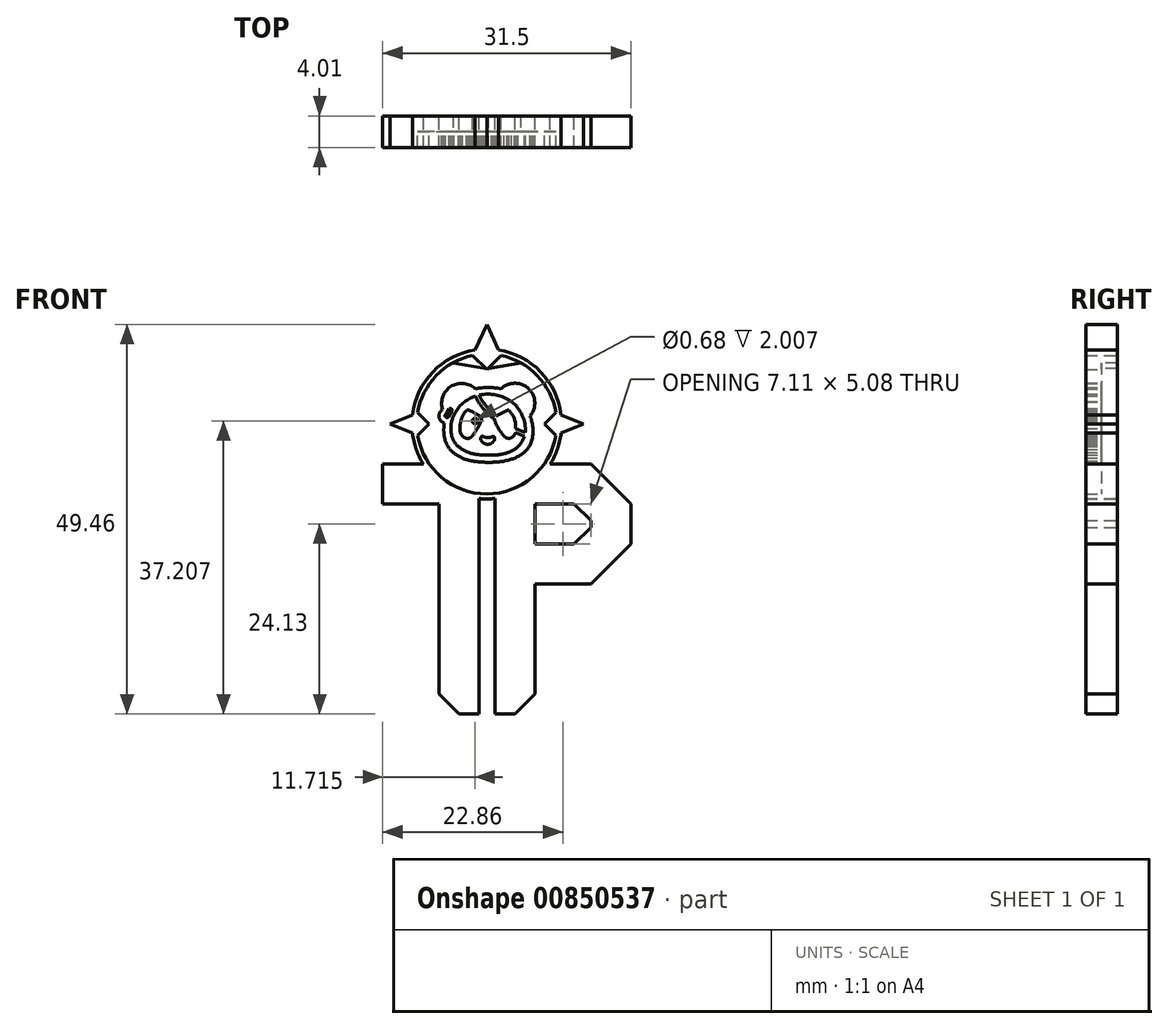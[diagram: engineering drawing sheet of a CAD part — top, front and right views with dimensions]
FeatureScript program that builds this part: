
annotation { "Feature Type Name" : "Feature", "Feature Type Description" : "" }
export const myFeature = defineFeature(function(context is Context, id is Id, definition is map)
    precondition{}
    {
        {
            var Q0;
            Q0=qCreatedBy(makeId("Front.planeOp"),FACE);
            var sketch = newSketch(context, id + "F0", { "sketchPlane" : qUnion([Q0])});
            skLineSegment(sketch, "E0.bottom", {"start": v(0, 0) * mm, "end": v(26.42, 0) * mm});
            skLineSegment(sketch, "E0.top", {"start": v(0, 31.75) * mm, "end": v(26.42, 31.75) * mm});
            skLineSegment(sketch, "E0.left", {"start": v(0, 0) * mm, "end": v(0, 31.75) * mm});
            skLineSegment(sketch, "E0.right", {"start": v(26.42, 0) * mm, "end": v(26.42, 16.5) * mm});
            skLineSegment(sketch, "E1", {"start": v(13.2, 31.75) * mm, "end": v(13.2, 0) * mm});
            skLineSegment(sketch, "E2", {"start": v(0, 26.67) * mm, "end": v(7.11, 26.67) * mm});
            skLineSegment(sketch, "E3", {"start": v(7.11, 26.67) * mm, "end": v(7.11, 0) * mm});
            skLineSegment(sketch, "E4", {"start": v(12.2, 31.75) * mm, "end": v(12.2, 0) * mm});
            skLineSegment(sketch, "E5", {"start": v(14.22, 31.75) * mm, "end": v(14.22, 0) * mm});
            skLineSegment(sketch, "E6", {"start": v(19.3, 31.75) * mm, "end": v(19.3, 0) * mm});
            skLineSegment(sketch, "E7", {"start": v(26.42, 31.75) * mm, "end": v(31.5, 26.67) * mm});
            skLineSegment(sketch, "E8", {"start": v(31.5, 26.67) * mm, "end": v(31.5, 21.59) * mm});
            skLineSegment(sketch, "E9", {"start": v(31.5, 21.59) * mm, "end": v(26.42, 16.5) * mm});
            skLineSegment(sketch, "E10", {"start": v(26.42, 16.5) * mm, "end": v(19.3, 16.5) * mm});
            skLineSegment(sketch, "E11", {"start": v(24.31, 26.67) * mm, "end": v(19.3, 26.67) * mm});
            skLineSegment(sketch, "E12", {"start": v(24.31, 21.59) * mm, "end": v(19.3, 21.59) * mm});
            skLineSegment(sketch, "E13.trimOffspring", {"start": v(26.42, 23.7) * mm, "end": v(26.42, 24.57) * mm});
            skLineSegment(sketch, "E14", {"start": v(24.31, 26.67) * mm, "end": v(26.42, 24.57) * mm});
            skLineSegment(sketch, "E15", {"start": v(24.31, 21.59) * mm, "end": v(26.42, 23.7) * mm});
            skPoint(sketch, "E16.orphan", {"position": v(26.42, 26.67) * mm});
            skPoint(sketch, "E17.orphan", {"position": v(26.42, 21.59) * mm});
            skLineSegment(sketch, "E18", {"start": v(0, 26.67) * mm, "end": v(0, 31.75) * mm});
            skLineSegment(sketch, "E19", {"start": v(0, 29.2) * mm, "end": v(2.54, 26.67) * mm});
            skLineSegment(sketch, "E20", {"start": v(7.11, 0) * mm, "end": v(12.2, 0) * mm});
            skLineSegment(sketch, "E21", {"start": v(14.22, 0) * mm, "end": v(19.3, 0) * mm});
            skLineSegment(sketch, "E22", {"start": v(9.65, 0) * mm, "end": v(7.11, 2.54) * mm});
            skLineSegment(sketch, "E23", {"start": v(16.76, 0) * mm, "end": v(19.3, 2.54) * mm});
            skCircle(sketch, "E24", {"center": v(13.2, 36.83) * mm, "radius": 9.53 * mm});
            skSolve(sketch);
        }
        {
            var Q0;
            {var subQ0=sQuery(id+"F0.wireOp",EDGE,"E24");var subQ1=sQuery(id+"F0.wireOp",EDGE,"E0.top");var subQ7=makeQuery(id+"F0.imprint","INTERSECT",VERTEX,{"disambiguationData":[OD(0.0)],"derivedFrom":[subQ1,subQ0]});Q0=makeQuery(id+"F0.imprint","IMPRINT",FACE,{"disambiguationData":[TD([[makeQuery(id+"F0.imprint","IMPRINT",EDGE,{"disambiguationData":[TD([[subQ7,-1.0]])],"derivedFrom":subQ1}),1.0]])]});}
            var Q1;
            {var subQ0=sQuery(id+"F0.wireOp",EDGE,"E24");var subQ1=sQuery(id+"F0.wireOp",EDGE,"E0.top");var subQ2=makeQuery(id+"F0.imprint","INTERSECT",VERTEX,{"disambiguationData":[OD(0.0)],"derivedFrom":[subQ1,subQ0]});Q1=makeQuery(id+"F0.imprint","IMPRINT",FACE,{"disambiguationData":[TD([[makeQuery(id+"F0.imprint","IMPRINT",EDGE,{"disambiguationData":[TD([[subQ2,-1.0]])],"derivedFrom":subQ1}),-1.0]])]});}
            var Q2;
            {var subQ0=sQuery(id+"F0.wireOp",EDGE,"E5");var subQ1=sQuery(id+"F0.wireOp",EDGE,"E0.top");var subQ2=makeQuery(id+"F0.imprint","INTERSECT",VERTEX,{"derivedFrom":[subQ1,subQ0]});Q2=makeQuery(id+"F0.imprint","IMPRINT",FACE,{"disambiguationData":[TD([[makeQuery(id+"F0.imprint","IMPRINT",EDGE,{"disambiguationData":[TD([[subQ2,-1.0]])],"derivedFrom":subQ1}),-1.0]])]});}
            var Q3;
            {var subQ0=sQuery(id+"F0.wireOp",EDGE,"E4");var subQ1=sQuery(id+"F0.wireOp",EDGE,"E0.top");var subQ2=makeQuery(id+"F0.imprint","INTERSECT",VERTEX,{"derivedFrom":[subQ1,subQ0]});Q3=makeQuery(id+"F0.imprint","IMPRINT",FACE,{"disambiguationData":[TD([[makeQuery(id+"F0.imprint","IMPRINT",EDGE,{"disambiguationData":[TD([[subQ2,-1.0]])],"derivedFrom":subQ1}),-1.0]])]});}
            var Q4;
            {var subQ0=sQuery(id+"F0.wireOp",EDGE,"E5");var subQ1=sQuery(id+"F0.wireOp",EDGE,"E0.top");var subQ2=makeQuery(id+"F0.imprint","INTERSECT",VERTEX,{"derivedFrom":[subQ1,subQ0]});Q4=makeQuery(id+"F0.imprint","IMPRINT",FACE,{"disambiguationData":[TD([[makeQuery(id+"F0.imprint","IMPRINT",EDGE,{"disambiguationData":[TD([[subQ2,1.0]])],"derivedFrom":subQ1}),-1.0]])]});}
            var Q5;
            {var subQ0=sQuery(id+"F0.wireOp",EDGE,"E19");Q5=makeQuery(id+"F0.imprint","IMPRINT",FACE,{"disambiguationData":[TD([[makeQuery(id+"F0.imprint","IMPRINT",EDGE,{"derivedFrom":subQ0}),1.0]])]});}
            var Q6;
            {var subQ8=sQuery(id+"F0.wireOp",EDGE,"E23");Q6=makeQuery(id+"F0.imprint","IMPRINT",FACE,{"disambiguationData":[TD([[makeQuery(id+"F0.imprint","IMPRINT",EDGE,{"derivedFrom":subQ8}),1.0]])]});}
            var Q7;
            {var subQ3=sQuery(id+"F0.wireOp",EDGE,"E7");Q7=makeQuery(id+"F0.imprint","IMPRINT",FACE,{"disambiguationData":[TD([[makeQuery(id+"F0.imprint","IMPRINT",EDGE,{"derivedFrom":subQ3}),-1.0]])]});}
            var Q8;
            {var subQ0=sQuery(id+"F0.wireOp",EDGE,"E24");var subQ1=sQuery(id+"F0.wireOp",EDGE,"E0.top");var subQ2=makeQuery(id+"F0.imprint","INTERSECT",VERTEX,{"disambiguationData":[OD(1.0)],"derivedFrom":[subQ1,subQ0]});Q8=makeQuery(id+"F0.imprint","IMPRINT",FACE,{"disambiguationData":[TD([[makeQuery(id+"F0.imprint","IMPRINT",EDGE,{"disambiguationData":[TD([[subQ2,1.0]])],"derivedFrom":subQ1}),-1.0]])]});}
            var Q9;
            {var subQ0=sQuery(id+"F0.wireOp",EDGE,"E19");Q9=makeQuery(id+"F0.imprint","IMPRINT",FACE,{"disambiguationData":[TD([[makeQuery(id+"F0.imprint","IMPRINT",EDGE,{"derivedFrom":subQ0}),-1.0]])]});}
            extrude(context, id + "F1", {"entities" : qUnion([Q0, Q1, Q2, Q3, Q4, Q5, Q6, Q7, Q8, Q9]), "depth" : 2 * mm, "offsetDistance" : 25.4 * mm});
        }
        {
            var Q0;
            Q0=makeQuery(id+"F1.opExtrude","CAP_FACE",FACE,{"disambiguationData":[OSD([sQuery(id+"F0.wireOp",EDGE,"E0.bottom"),sQuery(id+"F0.wireOp",EDGE,"E0.top"),sQuery(id+"F0.wireOp",EDGE,"E0.left"),sQuery(id+"F0.wireOp",EDGE,"E2"),sQuery(id+"F0.wireOp",EDGE,"E3"),sQuery(id+"F0.wireOp",EDGE,"E4"),sQuery(id+"F0.wireOp",EDGE,"E5"),sQuery(id+"F0.wireOp",EDGE,"E6"),sQuery(id+"F0.wireOp",EDGE,"E7"),sQuery(id+"F0.wireOp",EDGE,"E8"),sQuery(id+"F0.wireOp",EDGE,"E9"),sQuery(id+"F0.wireOp",EDGE,"E10"),sQuery(id+"F0.wireOp",EDGE,"E11"),sQuery(id+"F0.wireOp",EDGE,"E12"),sQuery(id+"F0.wireOp",EDGE,"E13.trimOffspring"),sQuery(id+"F0.wireOp",EDGE,"E14"),sQuery(id+"F0.wireOp",EDGE,"E15"),sQuery(id+"F0.wireOp",EDGE,"E22"),sQuery(id+"F0.wireOp",EDGE,"E23"),sQuery(id+"F0.wireOp",EDGE,"E24")])],"isStart":false});
            var sketch = newSketch(context, id + "F2", { "sketchPlane" : qUnion([Q0])});
            skLineSegment(sketch, "E25.bottom", {"start": v(0, 0) * mm, "end": v(26.42, 0) * mm});
            skLineSegment(sketch, "E25.top", {"start": v(0, 31.75) * mm, "end": v(26.42, 31.75) * mm});
            skLineSegment(sketch, "E25.left", {"start": v(0, 0) * mm, "end": v(0, 31.75) * mm});
            skLineSegment(sketch, "E25.right", {"start": v(26.42, 0) * mm, "end": v(26.42, 16.5) * mm});
            skLineSegment(sketch, "E26", {"start": v(13.2, 31.75) * mm, "end": v(13.2, 0) * mm});
            skLineSegment(sketch, "E27", {"start": v(0, 26.67) * mm, "end": v(7.11, 26.67) * mm});
            skLineSegment(sketch, "E28", {"start": v(7.11, 26.67) * mm, "end": v(7.11, 0) * mm});
            skLineSegment(sketch, "E29", {"start": v(12.2, 31.75) * mm, "end": v(12.2, 0) * mm});
            skLineSegment(sketch, "E30", {"start": v(14.22, 31.75) * mm, "end": v(14.22, 0) * mm});
            skLineSegment(sketch, "E31", {"start": v(19.3, 31.75) * mm, "end": v(19.3, 0) * mm});
            skLineSegment(sketch, "E32", {"start": v(26.42, 31.75) * mm, "end": v(31.5, 26.67) * mm});
            skLineSegment(sketch, "E33", {"start": v(31.5, 26.67) * mm, "end": v(31.5, 21.59) * mm});
            skLineSegment(sketch, "E34", {"start": v(31.5, 21.59) * mm, "end": v(26.42, 16.5) * mm});
            skLineSegment(sketch, "E35", {"start": v(26.42, 16.5) * mm, "end": v(19.3, 16.5) * mm});
            skLineSegment(sketch, "E36", {"start": v(24.31, 26.67) * mm, "end": v(19.3, 26.67) * mm});
            skLineSegment(sketch, "E37", {"start": v(24.31, 21.59) * mm, "end": v(19.3, 21.59) * mm});
            skLineSegment(sketch, "E38.trimOffspring", {"start": v(26.42, 23.7) * mm, "end": v(26.42, 24.57) * mm});
            skLineSegment(sketch, "E39", {"start": v(24.31, 26.67) * mm, "end": v(26.42, 24.57) * mm});
            skLineSegment(sketch, "E40", {"start": v(24.31, 21.59) * mm, "end": v(26.42, 23.7) * mm});
            skPoint(sketch, "E41.orphan", {"position": v(26.42, 26.67) * mm});
            skPoint(sketch, "E42.orphan", {"position": v(26.42, 21.59) * mm});
            skLineSegment(sketch, "E43", {"start": v(0, 26.67) * mm, "end": v(0, 31.75) * mm});
            skLineSegment(sketch, "E44", {"start": v(0, 29.2) * mm, "end": v(2.54, 26.67) * mm});
            skLineSegment(sketch, "E45", {"start": v(7.11, 0) * mm, "end": v(12.2, 0) * mm});
            skLineSegment(sketch, "E46", {"start": v(14.22, 0) * mm, "end": v(19.3, 0) * mm});
            skLineSegment(sketch, "E47", {"start": v(9.65, 0) * mm, "end": v(7.11, 2.54) * mm});
            skLineSegment(sketch, "E48", {"start": v(16.76, 0) * mm, "end": v(19.3, 2.54) * mm});
            skCircle(sketch, "E49", {"center": v(13.2, 36.83) * mm, "radius": 9.53 * mm});
            skArc(sketch, "E50", {"start": v(6.4, 36) * mm, "mid": v(6.22, 35.67) * mm, "end": v(6.11, 35.3) * mm});
            skArc(sketch, "E51", {"start": v(6.11, 35.3) * mm, "mid": v(6.1, 35.08) * mm, "end": v(6.16, 34.85) * mm});
            skArc(sketch, "E52", {"start": v(6.16, 34.85) * mm, "mid": v(6.22, 34.79) * mm, "end": v(6.3, 34.77) * mm});
            skArc(sketch, "E53", {"start": v(6.3, 34.77) * mm, "mid": v(6.4, 34.81) * mm, "end": v(6.47, 34.9) * mm});
            skArc(sketch, "E54", {"start": v(6.88, 35.33) * mm, "mid": v(6.66, 35.14) * mm, "end": v(6.47, 34.9) * mm});
            skArc(sketch, "E55", {"start": v(7.24, 35.54) * mm, "mid": v(7.06, 35.45) * mm, "end": v(6.88, 35.33) * mm});
            skArc(sketch, "E56", {"start": v(7.7, 35.67) * mm, "mid": v(7.47, 35.61) * mm, "end": v(7.24, 35.54) * mm});
            skArc(sketch, "E57", {"start": v(9.2, 36.34) * mm, "mid": v(8.98, 36.2) * mm, "end": v(8.78, 36.05) * mm});
            skArc(sketch, "E58", {"start": v(9.2, 36.34) * mm, "mid": v(9.36, 36.41) * mm, "end": v(9.52, 36.5) * mm});
            skArc(sketch, "E59", {"start": v(9.52, 36.5) * mm, "mid": v(10.37, 36.37) * mm, "end": v(11.23, 36.4) * mm});
            skArc(sketch, "E60", {"start": v(11.23, 36.4) * mm, "mid": v(11.72, 36.48) * mm, "end": v(12.19, 36.65) * mm});
            skArc(sketch, "E61", {"start": v(12.19, 36.65) * mm, "mid": v(12.45, 36.8) * mm, "end": v(12.66, 37.03) * mm});
            skArc(sketch, "E62", {"start": v(11.55, 37.03) * mm, "mid": v(12.1, 37.01) * mm, "end": v(12.66, 37.03) * mm});
            skArc(sketch, "E63", {"start": v(11.07, 37.17) * mm, "mid": v(11.3, 37.08) * mm, "end": v(11.55, 37.03) * mm});
            skArc(sketch, "E64", {"start": v(10.85, 37.36) * mm, "mid": v(10.95, 37.25) * mm, "end": v(11.07, 37.17) * mm});
            skArc(sketch, "E65", {"start": v(12.47, 37.67) * mm, "mid": v(11.65, 37.56) * mm, "end": v(10.85, 37.36) * mm});
            skArc(sketch, "E66", {"start": v(14.27, 37.6) * mm, "mid": v(13.38, 37.7) * mm, "end": v(12.47, 37.67) * mm});
            skArc(sketch, "E67", {"start": v(16.2, 36.98) * mm, "mid": v(15.26, 37.36) * mm, "end": v(14.27, 37.6) * mm});
            skArc(sketch, "E68", {"start": v(17.82, 36) * mm, "mid": v(17.02, 36.51) * mm, "end": v(16.2, 36.98) * mm});
            skArc(sketch, "E69", {"start": v(18.3, 35.54) * mm, "mid": v(18.08, 35.79) * mm, "end": v(17.82, 36) * mm});
            skArc(sketch, "E70", {"start": v(18.3, 35.54) * mm, "mid": v(18.28, 35.11) * mm, "end": v(18.33, 34.7) * mm});
            skArc(sketch, "E71", {"start": v(18.33, 34.7) * mm, "mid": v(18.49, 34.23) * mm, "end": v(18.74, 33.8) * mm});
            skArc(sketch, "E72", {"start": v(18.74, 33.8) * mm, "mid": v(18.9, 33.62) * mm, "end": v(19.08, 33.46) * mm});
            skArc(sketch, "E73", {"start": v(19.08, 33.46) * mm, "mid": v(19.2, 33.62) * mm, "end": v(19.3, 33.8) * mm});
            skArc(sketch, "E74", {"start": v(19.3, 33.8) * mm, "mid": v(19.42, 34.13) * mm, "end": v(19.47, 34.48) * mm});
            skArc(sketch, "E75", {"start": v(19.47, 34.48) * mm, "mid": v(19.48, 34.72) * mm, "end": v(19.47, 34.95) * mm});
            skArc(sketch, "E76", {"start": v(19.47, 34.95) * mm, "mid": v(19.88, 34.96) * mm, "end": v(20.3, 35) * mm});
            skArc(sketch, "E77", {"start": v(20.3, 35) * mm, "mid": v(20.67, 35.07) * mm, "end": v(21.02, 35.2) * mm});
            skArc(sketch, "E78", {"start": v(21.02, 35.2) * mm, "mid": v(21.2, 35.32) * mm, "end": v(21.35, 35.48) * mm});
            skArc(sketch, "E79", {"start": v(21.35, 35.48) * mm, "mid": v(20.95, 35.65) * mm, "end": v(20.53, 35.79) * mm});
            skArc(sketch, "E80", {"start": v(20.53, 35.79) * mm, "mid": v(20.12, 35.96) * mm, "end": v(19.7, 36.1) * mm});
            skArc(sketch, "E81", {"start": v(19.7, 36.1) * mm, "mid": v(19.33, 36.15) * mm, "end": v(18.97, 36.1) * mm});
            skArc(sketch, "E82", {"start": v(18.74, 36.12) * mm, "mid": v(18.85, 36.09) * mm, "end": v(18.97, 36.1) * mm});
            skArc(sketch, "E83", {"start": v(18.38, 36.54) * mm, "mid": v(18.54, 36.31) * mm, "end": v(18.74, 36.12) * mm});
            skArc(sketch, "E84", {"start": v(18.38, 36.54) * mm, "mid": v(17.88, 37.34) * mm, "end": v(17.35, 38.12) * mm});
            skArc(sketch, "E85", {"start": v(17.35, 38.12) * mm, "mid": v(16.5, 38.98) * mm, "end": v(15.51, 39.69) * mm});
            skArc(sketch, "E86", {"start": v(15.51, 39.69) * mm, "mid": v(14.75, 40.1) * mm, "end": v(13.95, 40.42) * mm});
            skArc(sketch, "E87", {"start": v(13.49, 40.82) * mm, "mid": v(13.7, 40.6) * mm, "end": v(13.95, 40.42) * mm});
            skArc(sketch, "E88", {"start": v(13.4, 41.11) * mm, "mid": v(13.42, 40.96) * mm, "end": v(13.49, 40.82) * mm});
            skArc(sketch, "E89", {"start": v(13.57, 41.38) * mm, "mid": v(13.45, 41.27) * mm, "end": v(13.4, 41.11) * mm});
            skArc(sketch, "E90", {"start": v(13.57, 41.38) * mm, "mid": v(13.77, 41.52) * mm, "end": v(13.95, 41.68) * mm});
            skArc(sketch, "E91", {"start": v(13.95, 41.68) * mm, "mid": v(14.07, 41.84) * mm, "end": v(14.14, 42.03) * mm});
            skArc(sketch, "E92", {"start": v(14.14, 42.03) * mm, "mid": v(13.9, 42.08) * mm, "end": v(13.64, 42.09) * mm});
            skArc(sketch, "E93", {"start": v(13.64, 42.09) * mm, "mid": v(13.3, 42.07) * mm, "end": v(12.97, 42) * mm});
            skArc(sketch, "E94", {"start": v(12.97, 42) * mm, "mid": v(12.34, 41.75) * mm, "end": v(11.78, 41.38) * mm});
            skArc(sketch, "E95", {"start": v(11.78, 41.38) * mm, "mid": v(11.32, 40.98) * mm, "end": v(10.92, 40.5) * mm});
            skArc(sketch, "E96", {"start": v(10.92, 40.5) * mm, "mid": v(9.67, 40.25) * mm, "end": v(8.5, 39.73) * mm});
            skArc(sketch, "E97", {"start": v(8.5, 39.73) * mm, "mid": v(7.74, 39.11) * mm, "end": v(7.14, 38.35) * mm});
            skArc(sketch, "E98", {"start": v(7.14, 38.35) * mm, "mid": v(6.66, 37.56) * mm, "end": v(6.37, 36.7) * mm});
            skArc(sketch, "E99", {"start": v(6.37, 36.7) * mm, "mid": v(6.34, 36.35) * mm, "end": v(6.4, 36) * mm});
            skArc(sketch, "E100", {"start": v(8.47, 38.82) * mm, "mid": v(7.96, 38.3) * mm, "end": v(7.62, 37.67) * mm});
            skArc(sketch, "E101", {"start": v(9.85, 39.52) * mm, "mid": v(9.13, 39.23) * mm, "end": v(8.47, 38.82) * mm});
            skArc(sketch, "E102", {"start": v(11.05, 39.73) * mm, "mid": v(10.44, 39.66) * mm, "end": v(9.85, 39.52) * mm});
            skArc(sketch, "E103", {"start": v(8.43, 38.6) * mm, "mid": v(8, 38.16) * mm, "end": v(7.62, 37.67) * mm});
            skArc(sketch, "E104", {"start": v(9.45, 39.2) * mm, "mid": v(8.92, 38.94) * mm, "end": v(8.43, 38.6) * mm});
            skArc(sketch, "E105", {"start": v(11.05, 39.73) * mm, "mid": v(10.24, 39.5) * mm, "end": v(9.45, 39.2) * mm});
            skArc(sketch, "E106", {"start": v(7.7, 35.67) * mm, "mid": v(8.27, 35.77) * mm, "end": v(8.78, 36.05) * mm});
            skSolve(sketch);
        }
        {
            var Q0;
            {var subQ12=sQuery(id+"F2.wireOp",EDGE,"E44");Q0=makeQuery(id+"F2.imprint","IMPRINT",FACE,{"disambiguationData":[TD([[makeQuery(id+"F2.imprint","IMPRINT",EDGE,{"derivedFrom":subQ12}),1.0]])]});}
            var Q1;
            {var subQ6=sQuery(id+"F2.wireOp",EDGE,"E48");Q1=makeQuery(id+"F2.imprint","IMPRINT",FACE,{"disambiguationData":[TD([[makeQuery(id+"F2.imprint","IMPRINT",EDGE,{"derivedFrom":subQ6}),1.0]])]});}
            var Q2;
            {var subQ2=sQuery(id+"F2.wireOp",EDGE,"E32");Q2=makeQuery(id+"F2.imprint","IMPRINT",FACE,{"disambiguationData":[TD([[makeQuery(id+"F2.imprint","IMPRINT",EDGE,{"derivedFrom":subQ2}),-1.0]])]});}
            var Q3;
            {var subQ3=sQuery(id+"F2.wireOp",EDGE,"E44");Q3=makeQuery(id+"F2.imprint","IMPRINT",FACE,{"disambiguationData":[TD([[makeQuery(id+"F2.imprint","IMPRINT",EDGE,{"derivedFrom":subQ3}),-1.0]])]});}
            extrude(context, id + "F3", {"entities" : qUnion([Q0, Q1, Q2, Q3]), "operationType" : NewBodyOperationType.ADD, "depth" : 2 * mm, "offsetDistance" : 25.4 * mm});
        }
        {
            var Q0;
            Q0=makeQuery(id+"F1.opExtrude","CAP_FACE",FACE,{"disambiguationData":[OSD([sQuery(id+"F0.wireOp",EDGE,"E0.bottom"),sQuery(id+"F0.wireOp",EDGE,"E0.top"),sQuery(id+"F0.wireOp",EDGE,"E0.left"),sQuery(id+"F0.wireOp",EDGE,"E2"),sQuery(id+"F0.wireOp",EDGE,"E3"),sQuery(id+"F0.wireOp",EDGE,"E4"),sQuery(id+"F0.wireOp",EDGE,"E5"),sQuery(id+"F0.wireOp",EDGE,"E6"),sQuery(id+"F0.wireOp",EDGE,"E7"),sQuery(id+"F0.wireOp",EDGE,"E8"),sQuery(id+"F0.wireOp",EDGE,"E9"),sQuery(id+"F0.wireOp",EDGE,"E10"),sQuery(id+"F0.wireOp",EDGE,"E11"),sQuery(id+"F0.wireOp",EDGE,"E12"),sQuery(id+"F0.wireOp",EDGE,"E13.trimOffspring"),sQuery(id+"F0.wireOp",EDGE,"E14"),sQuery(id+"F0.wireOp",EDGE,"E15"),sQuery(id+"F0.wireOp",EDGE,"E22"),sQuery(id+"F0.wireOp",EDGE,"E23"),sQuery(id+"F0.wireOp",EDGE,"E24")])],"isStart":false});
            var sketch = newSketch(context, id + "F4", { "sketchPlane" : qUnion([Q0])});
            skLineSegment(sketch, "E107.bottom", {"start": v(0, 0) * mm, "end": v(26.42, 0) * mm});
            skLineSegment(sketch, "E107.top", {"start": v(0, 31.75) * mm, "end": v(26.42, 31.75) * mm});
            skLineSegment(sketch, "E107.left", {"start": v(0, 0) * mm, "end": v(0, 31.75) * mm});
            skLineSegment(sketch, "E107.right", {"start": v(26.42, 0) * mm, "end": v(26.42, 16.5) * mm});
            skLineSegment(sketch, "E108", {"start": v(13.2, 31.75) * mm, "end": v(13.2, 0) * mm});
            skLineSegment(sketch, "E109", {"start": v(0, 26.67) * mm, "end": v(7.11, 26.67) * mm});
            skLineSegment(sketch, "E110", {"start": v(7.11, 26.67) * mm, "end": v(7.11, 0) * mm});
            skLineSegment(sketch, "E111", {"start": v(12.2, 31.75) * mm, "end": v(12.2, 0) * mm});
            skLineSegment(sketch, "E112", {"start": v(14.22, 31.75) * mm, "end": v(14.22, 0) * mm});
            skLineSegment(sketch, "E113", {"start": v(19.3, 31.75) * mm, "end": v(19.3, 0) * mm});
            skLineSegment(sketch, "E114", {"start": v(26.42, 31.75) * mm, "end": v(31.5, 26.67) * mm});
            skLineSegment(sketch, "E115", {"start": v(31.5, 26.67) * mm, "end": v(31.5, 21.59) * mm});
            skLineSegment(sketch, "E116", {"start": v(31.5, 21.59) * mm, "end": v(26.42, 16.5) * mm});
            skLineSegment(sketch, "E117", {"start": v(26.42, 16.5) * mm, "end": v(19.3, 16.5) * mm});
            skLineSegment(sketch, "E118", {"start": v(24.31, 26.67) * mm, "end": v(19.3, 26.67) * mm});
            skLineSegment(sketch, "E119", {"start": v(24.31, 21.59) * mm, "end": v(19.3, 21.59) * mm});
            skLineSegment(sketch, "E120.trimOffspring", {"start": v(26.42, 23.7) * mm, "end": v(26.42, 24.57) * mm});
            skLineSegment(sketch, "E121", {"start": v(24.31, 26.67) * mm, "end": v(26.42, 24.57) * mm});
            skLineSegment(sketch, "E122", {"start": v(24.31, 21.59) * mm, "end": v(26.42, 23.7) * mm});
            skPoint(sketch, "E123.orphan", {"position": v(26.42, 26.67) * mm});
            skPoint(sketch, "E124.orphan", {"position": v(26.42, 21.59) * mm});
            skLineSegment(sketch, "E125", {"start": v(0, 26.67) * mm, "end": v(0, 31.75) * mm});
            skLineSegment(sketch, "E126", {"start": v(0, 29.2) * mm, "end": v(2.54, 26.67) * mm});
            skLineSegment(sketch, "E127", {"start": v(7.11, 0) * mm, "end": v(12.2, 0) * mm});
            skLineSegment(sketch, "E128", {"start": v(14.22, 0) * mm, "end": v(19.3, 0) * mm});
            skLineSegment(sketch, "E129", {"start": v(9.65, 0) * mm, "end": v(7.11, 2.54) * mm});
            skLineSegment(sketch, "E130", {"start": v(16.76, 0) * mm, "end": v(19.3, 2.54) * mm});
            skCircle(sketch, "E131", {"center": v(13.2, 36.83) * mm, "radius": 9.53 * mm});
            skCircle(sketch, "E132", {"center": v(13.2, 36.83) * mm, "radius": 8.9 * mm});
            skLineSegment(sketch, "E133", {"start": v(13.2, 36.83) * mm, "end": v(22.73, 36.83) * mm});
            skLineSegment(sketch, "E134", {"start": v(13.2, 36.83) * mm, "end": v(13.2, 46.35) * mm});
            skLineSegment(sketch, "E135", {"start": v(13.2, 36.83) * mm, "end": v(3.68, 36.83) * mm});
            skLineSegment(sketch, "E136", {"start": v(13.2, 43.74) * mm, "end": v(11.41, 45.54) * mm});
            skLineSegment(sketch, "E137", {"start": v(13.2, 43.74) * mm, "end": v(15, 45.54) * mm});
            skLineSegment(sketch, "E138", {"start": v(11.41, 45.54) * mm, "end": v(13.2, 49.46) * mm});
            skLineSegment(sketch, "E139", {"start": v(13.2, 49.46) * mm, "end": v(15, 45.54) * mm});
            skLineSegment(sketch, "E140", {"start": v(13.2, 49.46) * mm, "end": v(13.2, 46.35) * mm});
            skLineSegment(sketch, "E141", {"start": v(20.54, 36.83) * mm, "end": v(21.98, 38.27) * mm});
            skLineSegment(sketch, "E142", {"start": v(20.54, 36.83) * mm, "end": v(21.98, 35.4) * mm});
            skLineSegment(sketch, "E143", {"start": v(21.98, 38.27) * mm, "end": v(25.5, 36.83) * mm});
            skLineSegment(sketch, "E144", {"start": v(21.98, 35.4) * mm, "end": v(25.5, 36.83) * mm});
            skLineSegment(sketch, "E145", {"start": v(22.73, 36.83) * mm, "end": v(25.5, 36.83) * mm});
            skLineSegment(sketch, "E146", {"start": v(5.87, 36.83) * mm, "end": v(4.43, 38.27) * mm});
            skLineSegment(sketch, "E147", {"start": v(5.87, 36.83) * mm, "end": v(4.43, 35.4) * mm});
            skLineSegment(sketch, "E148", {"start": v(4.43, 35.4) * mm, "end": v(0.9, 36.83) * mm});
            skLineSegment(sketch, "E149", {"start": v(0.9, 36.83) * mm, "end": v(4.43, 38.27) * mm});
            skLineSegment(sketch, "E150", {"start": v(3.68, 36.83) * mm, "end": v(0.9, 36.83) * mm});
            skSolve(sketch);
        }
        {
            var Q0;
            {var subQ0=sQuery(id+"F4.wireOp",EDGE,"E138");var subQ1=sQuery(id+"F4.wireOp",EDGE,"E131");var subQ2=makeQuery(id+"F4.imprint","INTERSECT",VERTEX,{"derivedFrom":[subQ1,subQ0]});Q0=makeQuery(id+"F4.imprint","IMPRINT",FACE,{"disambiguationData":[TD([[makeQuery(id+"F4.imprint","IMPRINT",EDGE,{"disambiguationData":[TD([[subQ2,-1.0]])],"derivedFrom":subQ1}),1.0]])]});}
            var Q1;
            {var subQ0=sQuery(id+"F4.wireOp",EDGE,"E140");Q1=makeQuery(id+"F4.imprint","IMPRINT",FACE,{"disambiguationData":[TD([[makeQuery(id+"F4.imprint","IMPRINT",EDGE,{"derivedFrom":subQ0}),-1.0]])]});}
            var Q2;
            {var subQ1=sQuery(id+"F4.wireOp",EDGE,"E131");var subQ3=sQuery(id+"F4.wireOp",EDGE,"E138");var subQ4=makeQuery(id+"F4.imprint","INTERSECT",VERTEX,{"derivedFrom":[subQ1,subQ3]});Q2=makeQuery(id+"F4.imprint","IMPRINT",FACE,{"disambiguationData":[TD([[makeQuery(id+"F4.imprint","IMPRINT",EDGE,{"disambiguationData":[TD([[subQ4,1.0]])],"derivedFrom":subQ1}),1.0]])]});}
            var Q3;
            {var subQ0=sQuery(id+"F4.wireOp",EDGE,"E140");Q3=makeQuery(id+"F4.imprint","IMPRINT",FACE,{"disambiguationData":[TD([[makeQuery(id+"F4.imprint","IMPRINT",EDGE,{"derivedFrom":subQ0}),1.0]])]});}
            var Q4;
            {var subQ1=sQuery(id+"F4.wireOp",EDGE,"E131");var subQ3=sQuery(id+"F4.wireOp",EDGE,"E139");var subQ4=makeQuery(id+"F4.imprint","INTERSECT",VERTEX,{"derivedFrom":[subQ1,subQ3]});Q4=makeQuery(id+"F4.imprint","IMPRINT",FACE,{"disambiguationData":[TD([[makeQuery(id+"F4.imprint","IMPRINT",EDGE,{"disambiguationData":[TD([[subQ4,-1.0]])],"derivedFrom":subQ1}),1.0]])]});}
            var Q5;
            {var subQ0=sQuery(id+"F4.wireOp",EDGE,"E143");var subQ1=sQuery(id+"F4.wireOp",EDGE,"E131");var subQ2=makeQuery(id+"F4.imprint","INTERSECT",VERTEX,{"derivedFrom":[subQ1,subQ0]});Q5=makeQuery(id+"F4.imprint","IMPRINT",FACE,{"disambiguationData":[TD([[makeQuery(id+"F4.imprint","IMPRINT",EDGE,{"disambiguationData":[TD([[subQ2,-1.0]])],"derivedFrom":subQ1}),1.0]])]});}
            var Q6;
            {var subQ0=sQuery(id+"F4.wireOp",EDGE,"E145");Q6=makeQuery(id+"F4.imprint","IMPRINT",FACE,{"disambiguationData":[TD([[makeQuery(id+"F4.imprint","IMPRINT",EDGE,{"derivedFrom":subQ0}),1.0]])]});}
            var Q7;
            {var subQ0=sQuery(id+"F4.wireOp",EDGE,"E145");Q7=makeQuery(id+"F4.imprint","IMPRINT",FACE,{"disambiguationData":[TD([[makeQuery(id+"F4.imprint","IMPRINT",EDGE,{"derivedFrom":subQ0}),-1.0]])]});}
            var Q8;
            {var subQ1=sQuery(id+"F4.wireOp",EDGE,"E131");var subQ3=sQuery(id+"F4.wireOp",EDGE,"E143");var subQ4=makeQuery(id+"F4.imprint","INTERSECT",VERTEX,{"derivedFrom":[subQ1,subQ3]});Q8=makeQuery(id+"F4.imprint","IMPRINT",FACE,{"disambiguationData":[TD([[makeQuery(id+"F4.imprint","IMPRINT",EDGE,{"disambiguationData":[TD([[subQ4,1.0]])],"derivedFrom":subQ1}),1.0]])]});}
            var Q9;
            {var subQ1=sQuery(id+"F4.wireOp",EDGE,"E131");var subQ3=sQuery(id+"F4.wireOp",EDGE,"E144");var subQ4=makeQuery(id+"F4.imprint","INTERSECT",VERTEX,{"derivedFrom":[subQ1,subQ3]});Q9=makeQuery(id+"F4.imprint","IMPRINT",FACE,{"disambiguationData":[TD([[makeQuery(id+"F4.imprint","IMPRINT",EDGE,{"disambiguationData":[TD([[subQ4,-1.0]])],"derivedFrom":subQ1}),1.0]])]});}
            var Q10;
            {var subQ0=sQuery(id+"F4.wireOp",EDGE,"E131");var subQ1=sQuery(id+"F4.wireOp",EDGE,"E107.top");var subQ2=makeQuery(id+"F4.imprint","INTERSECT",VERTEX,{"disambiguationData":[OD(1.0)],"derivedFrom":[subQ1,subQ0]});Q10=makeQuery(id+"F4.imprint","IMPRINT",FACE,{"disambiguationData":[TD([[makeQuery(id+"F4.imprint","IMPRINT",EDGE,{"disambiguationData":[TD([[subQ2,1.0]])],"derivedFrom":subQ1}),1.0]])]});}
            var Q11;
            {var subQ0=sQuery(id+"F4.wireOp",EDGE,"E142");Q11=makeQuery(id+"F4.imprint","IMPRINT",FACE,{"disambiguationData":[TD([[makeQuery(id+"F4.imprint","IMPRINT",EDGE,{"derivedFrom":subQ0}),1.0]])]});}
            var Q12;
            {var subQ0=sQuery(id+"F4.wireOp",EDGE,"E141");Q12=makeQuery(id+"F4.imprint","IMPRINT",FACE,{"disambiguationData":[TD([[makeQuery(id+"F4.imprint","IMPRINT",EDGE,{"derivedFrom":subQ0}),-1.0]])]});}
            var Q13;
            {var subQ0=sQuery(id+"F4.wireOp",EDGE,"E136");Q13=makeQuery(id+"F4.imprint","IMPRINT",FACE,{"disambiguationData":[TD([[makeQuery(id+"F4.imprint","IMPRINT",EDGE,{"derivedFrom":subQ0}),-1.0]])]});}
            var Q14;
            {var subQ0=sQuery(id+"F4.wireOp",EDGE,"E137");Q14=makeQuery(id+"F4.imprint","IMPRINT",FACE,{"disambiguationData":[TD([[makeQuery(id+"F4.imprint","IMPRINT",EDGE,{"derivedFrom":subQ0}),1.0]])]});}
            var Q15;
            {var subQ0=sQuery(id+"F4.wireOp",EDGE,"E131");var subQ1=sQuery(id+"F4.wireOp",EDGE,"E107.top");var subQ2=makeQuery(id+"F4.imprint","INTERSECT",VERTEX,{"disambiguationData":[OD(1.0)],"derivedFrom":[subQ1,subQ0]});Q15=makeQuery(id+"F4.imprint","IMPRINT",FACE,{"disambiguationData":[TD([[makeQuery(id+"F4.imprint","IMPRINT",EDGE,{"disambiguationData":[TD([[subQ2,1.0]])],"derivedFrom":subQ1}),-1.0]])]});}
            var Q16;
            {var subQ0=sQuery(id+"F4.wireOp",EDGE,"E131");var subQ1=sQuery(id+"F4.wireOp",EDGE,"E112");var subQ2=makeQuery(id+"F4.imprint","INTERSECT",VERTEX,{"derivedFrom":[subQ1,subQ0]});Q16=makeQuery(id+"F4.imprint","IMPRINT",FACE,{"disambiguationData":[TD([[makeQuery(id+"F4.imprint","IMPRINT",EDGE,{"disambiguationData":[TD([[subQ2,1.0]])],"derivedFrom":subQ1}),1.0]])]});}
            var Q17;
            {var subQ0=sQuery(id+"F4.wireOp",EDGE,"E132");var subQ1=sQuery(id+"F4.wireOp",EDGE,"E108");var subQ2=makeQuery(id+"F4.imprint","INTERSECT",VERTEX,{"derivedFrom":[subQ1,subQ0]});Q17=makeQuery(id+"F4.imprint","IMPRINT",FACE,{"disambiguationData":[TD([[makeQuery(id+"F4.imprint","IMPRINT",EDGE,{"disambiguationData":[TD([[subQ2,-1.0]])],"derivedFrom":subQ1}),1.0]])]});}
            var Q18;
            {var subQ0=sQuery(id+"F4.wireOp",EDGE,"E132");var subQ1=sQuery(id+"F4.wireOp",EDGE,"E108");var subQ2=makeQuery(id+"F4.imprint","INTERSECT",VERTEX,{"derivedFrom":[subQ1,subQ0]});Q18=makeQuery(id+"F4.imprint","IMPRINT",FACE,{"disambiguationData":[TD([[makeQuery(id+"F4.imprint","IMPRINT",EDGE,{"disambiguationData":[TD([[subQ2,-1.0]])],"derivedFrom":subQ1}),-1.0]])]});}
            var Q19;
            {var subQ0=sQuery(id+"F4.wireOp",EDGE,"E131");var subQ1=sQuery(id+"F4.wireOp",EDGE,"E107.top");var subQ2=makeQuery(id+"F4.imprint","INTERSECT",VERTEX,{"disambiguationData":[OD(0.0)],"derivedFrom":[subQ1,subQ0]});Q19=makeQuery(id+"F4.imprint","IMPRINT",FACE,{"disambiguationData":[TD([[makeQuery(id+"F4.imprint","IMPRINT",EDGE,{"disambiguationData":[TD([[subQ2,-1.0]])],"derivedFrom":subQ1}),-1.0]])]});}
            var Q20;
            {var subQ0=sQuery(id+"F4.wireOp",EDGE,"E131");var subQ1=sQuery(id+"F4.wireOp",EDGE,"E107.top");var subQ2=makeQuery(id+"F4.imprint","INTERSECT",VERTEX,{"disambiguationData":[OD(0.0)],"derivedFrom":[subQ1,subQ0]});Q20=makeQuery(id+"F4.imprint","IMPRINT",FACE,{"disambiguationData":[TD([[makeQuery(id+"F4.imprint","IMPRINT",EDGE,{"disambiguationData":[TD([[subQ2,-1.0]])],"derivedFrom":subQ1}),1.0]])]});}
            var Q21;
            {var subQ0=sQuery(id+"F4.wireOp",EDGE,"E147");Q21=makeQuery(id+"F4.imprint","IMPRINT",FACE,{"disambiguationData":[TD([[makeQuery(id+"F4.imprint","IMPRINT",EDGE,{"derivedFrom":subQ0}),-1.0]])]});}
            var Q22;
            {var subQ0=sQuery(id+"F4.wireOp",EDGE,"E146");Q22=makeQuery(id+"F4.imprint","IMPRINT",FACE,{"disambiguationData":[TD([[makeQuery(id+"F4.imprint","IMPRINT",EDGE,{"derivedFrom":subQ0}),1.0]])]});}
            var Q23;
            {var subQ1=sQuery(id+"F4.wireOp",EDGE,"E131");var subQ3=sQuery(id+"F4.wireOp",EDGE,"E149");var subQ4=makeQuery(id+"F4.imprint","INTERSECT",VERTEX,{"derivedFrom":[subQ1,subQ3]});Q23=makeQuery(id+"F4.imprint","IMPRINT",FACE,{"disambiguationData":[TD([[makeQuery(id+"F4.imprint","IMPRINT",EDGE,{"disambiguationData":[TD([[subQ4,-1.0]])],"derivedFrom":subQ1}),1.0]])]});}
            var Q24;
            {var subQ1=sQuery(id+"F4.wireOp",EDGE,"E131");var subQ3=sQuery(id+"F4.wireOp",EDGE,"E148");var subQ4=makeQuery(id+"F4.imprint","INTERSECT",VERTEX,{"derivedFrom":[subQ1,subQ3]});Q24=makeQuery(id+"F4.imprint","IMPRINT",FACE,{"disambiguationData":[TD([[makeQuery(id+"F4.imprint","IMPRINT",EDGE,{"disambiguationData":[TD([[subQ4,1.0]])],"derivedFrom":subQ1}),1.0]])]});}
            var Q25;
            {var subQ0=sQuery(id+"F4.wireOp",EDGE,"E150");Q25=makeQuery(id+"F4.imprint","IMPRINT",FACE,{"disambiguationData":[TD([[makeQuery(id+"F4.imprint","IMPRINT",EDGE,{"derivedFrom":subQ0}),1.0]])]});}
            var Q26;
            {var subQ0=sQuery(id+"F4.wireOp",EDGE,"E150");Q26=makeQuery(id+"F4.imprint","IMPRINT",FACE,{"disambiguationData":[TD([[makeQuery(id+"F4.imprint","IMPRINT",EDGE,{"derivedFrom":subQ0}),-1.0]])]});}
            extrude(context, id + "F5", {"entities" : qUnion([Q0, Q1, Q2, Q3, Q4, Q5, Q6, Q7, Q8, Q9, Q10, Q11, Q12, Q13, Q14, Q15, Q16, Q17, Q18, Q19, Q20, Q21, Q22, Q23, Q24, Q25, Q26]), "operationType" : NewBodyOperationType.ADD, "depth" : 2 * mm, "offsetDistance" : 25.4 * mm});
        }
        {
            var Q0;
            {var subQ0=sQuery(id+"F4.wireOp",EDGE,"E138");var subQ1=sQuery(id+"F4.wireOp",EDGE,"E131");var subQ2=sQuery(id+"F4.wireOp",EDGE,"E149");var subQ3=sQuery(id+"F4.wireOp",EDGE,"E143");var subQ4=sQuery(id+"F4.wireOp",EDGE,"E139");var subQ7=sQuery(id+"F4.wireOp",EDGE,"E144");var subQ13=sQuery(id+"F4.wireOp",EDGE,"E148");Q0=makeQuery(id+"F5.boolean.opBoolean","SPLIT",FACE,{"disambiguationData":[TD([makeQuery(id+"F5.opExtrude","SWEPT_FACE",FACE,{"disambiguationData":[OSD([subQ3])]})])],"derivedFrom":makeQuery(id+"F5.opExtrude","CAP_FACE",FACE,{"disambiguationData":[OSD([subQ1,sQuery(id+"F4.wireOp",EDGE,"E132"),sQuery(id+"F4.wireOp",EDGE,"E136"),sQuery(id+"F4.wireOp",EDGE,"E137"),subQ0,subQ4,sQuery(id+"F4.wireOp",EDGE,"E141"),sQuery(id+"F4.wireOp",EDGE,"E142"),subQ3,subQ7,sQuery(id+"F4.wireOp",EDGE,"E146"),sQuery(id+"F4.wireOp",EDGE,"E147"),subQ13,subQ2])],"isStart":true})});}
            var Q1;
            {var subQ0=sQuery(id+"F4.wireOp",EDGE,"E138");var subQ1=sQuery(id+"F4.wireOp",EDGE,"E131");var subQ2=sQuery(id+"F4.wireOp",EDGE,"E149");var subQ3=sQuery(id+"F4.wireOp",EDGE,"E143");var subQ4=sQuery(id+"F4.wireOp",EDGE,"E139");var subQ7=sQuery(id+"F4.wireOp",EDGE,"E144");var subQ13=sQuery(id+"F4.wireOp",EDGE,"E148");Q1=makeQuery(id+"F5.boolean.opBoolean","SPLIT",FACE,{"disambiguationData":[TD([makeQuery(id+"F5.opExtrude","SWEPT_FACE",FACE,{"disambiguationData":[OSD([subQ0])]})])],"derivedFrom":makeQuery(id+"F5.opExtrude","CAP_FACE",FACE,{"disambiguationData":[OSD([subQ1,sQuery(id+"F4.wireOp",EDGE,"E132"),sQuery(id+"F4.wireOp",EDGE,"E136"),sQuery(id+"F4.wireOp",EDGE,"E137"),subQ0,subQ4,sQuery(id+"F4.wireOp",EDGE,"E141"),sQuery(id+"F4.wireOp",EDGE,"E142"),subQ3,subQ7,sQuery(id+"F4.wireOp",EDGE,"E146"),sQuery(id+"F4.wireOp",EDGE,"E147"),subQ13,subQ2])],"isStart":true})});}
            var Q2;
            {var subQ0=sQuery(id+"F4.wireOp",EDGE,"E138");var subQ1=sQuery(id+"F4.wireOp",EDGE,"E131");var subQ2=sQuery(id+"F4.wireOp",EDGE,"E149");var subQ3=sQuery(id+"F4.wireOp",EDGE,"E143");var subQ4=sQuery(id+"F4.wireOp",EDGE,"E139");var subQ7=sQuery(id+"F4.wireOp",EDGE,"E144");var subQ13=sQuery(id+"F4.wireOp",EDGE,"E148");Q2=makeQuery(id+"F5.boolean.opBoolean","SPLIT",FACE,{"disambiguationData":[TD([makeQuery(id+"F5.opExtrude","SWEPT_FACE",FACE,{"disambiguationData":[OSD([subQ13])]})])],"derivedFrom":makeQuery(id+"F5.opExtrude","CAP_FACE",FACE,{"disambiguationData":[OSD([subQ1,sQuery(id+"F4.wireOp",EDGE,"E132"),sQuery(id+"F4.wireOp",EDGE,"E136"),sQuery(id+"F4.wireOp",EDGE,"E137"),subQ0,subQ4,sQuery(id+"F4.wireOp",EDGE,"E141"),sQuery(id+"F4.wireOp",EDGE,"E142"),subQ3,subQ7,sQuery(id+"F4.wireOp",EDGE,"E146"),sQuery(id+"F4.wireOp",EDGE,"E147"),subQ13,subQ2])],"isStart":true})});}
            extrude(context, id + "F6", {"entities" : qUnion([Q0, Q1, Q2]), "operationType" : NewBodyOperationType.ADD, "depth" : 2 * mm, "offsetDistance" : 25.4 * mm});
        }
        {
            var Q0;
            Q0=makeQuery(id+"F1.opExtrude","CAP_FACE",FACE,{"disambiguationData":[OSD([sQuery(id+"F0.wireOp",EDGE,"E0.bottom"),sQuery(id+"F0.wireOp",EDGE,"E0.top"),sQuery(id+"F0.wireOp",EDGE,"E0.left"),sQuery(id+"F0.wireOp",EDGE,"E2"),sQuery(id+"F0.wireOp",EDGE,"E3"),sQuery(id+"F0.wireOp",EDGE,"E4"),sQuery(id+"F0.wireOp",EDGE,"E5"),sQuery(id+"F0.wireOp",EDGE,"E6"),sQuery(id+"F0.wireOp",EDGE,"E7"),sQuery(id+"F0.wireOp",EDGE,"E8"),sQuery(id+"F0.wireOp",EDGE,"E9"),sQuery(id+"F0.wireOp",EDGE,"E10"),sQuery(id+"F0.wireOp",EDGE,"E11"),sQuery(id+"F0.wireOp",EDGE,"E12"),sQuery(id+"F0.wireOp",EDGE,"E13.trimOffspring"),sQuery(id+"F0.wireOp",EDGE,"E14"),sQuery(id+"F0.wireOp",EDGE,"E15"),sQuery(id+"F0.wireOp",EDGE,"E22"),sQuery(id+"F0.wireOp",EDGE,"E23"),sQuery(id+"F0.wireOp",EDGE,"E24")])],"isStart":false});
            var sketch = newSketch(context, id + "F7", { "sketchPlane" : qUnion([Q0])});
            skArc(sketch, "E151", {"start": v(8.43, 41.44) * mm, "mid": v(7.59, 40.18) * mm, "end": v(7.6, 38.67) * mm});
            skArc(sketch, "E152", {"start": v(11.77, 41.3) * mm, "mid": v(10.12, 41.99) * mm, "end": v(8.43, 41.44) * mm});
            skArc(sketch, "E153", {"start": v(15, 41.3) * mm, "mid": v(13.39, 41.47) * mm, "end": v(11.77, 41.3) * mm});
            skArc(sketch, "E154", {"start": v(17.19, 41.98) * mm, "mid": v(16.02, 41.89) * mm, "end": v(15, 41.3) * mm});
            skArc(sketch, "E155", {"start": v(19.14, 40.41) * mm, "mid": v(18.37, 41.45) * mm, "end": v(17.19, 41.98) * mm});
            skArc(sketch, "E156", {"start": v(18.72, 37.86) * mm, "mid": v(19.28, 39.08) * mm, "end": v(19.14, 40.41) * mm});
            skArc(sketch, "E157", {"start": v(18.83, 34.44) * mm, "mid": v(19.07, 36.16) * mm, "end": v(18.72, 37.86) * mm});
            skArc(sketch, "E158", {"start": v(16.85, 32.54) * mm, "mid": v(18.03, 33.3) * mm, "end": v(18.83, 34.44) * mm});
            skArc(sketch, "E159", {"start": v(14.08, 31.97) * mm, "mid": v(15.5, 32.12) * mm, "end": v(16.85, 32.54) * mm});
            skArc(sketch, "E160", {"start": v(11.27, 32.12) * mm, "mid": v(12.67, 31.98) * mm, "end": v(14.08, 31.97) * mm});
            skPoint(sketch, "E160.startSnap0", {"position": v(15.5, 32.12) * mm});
            skArc(sketch, "E161", {"start": v(8.93, 33.24) * mm, "mid": v(10.03, 32.54) * mm, "end": v(11.27, 32.12) * mm});
            skArc(sketch, "E162", {"start": v(7.83, 35.18) * mm, "mid": v(8.2, 34.1) * mm, "end": v(8.93, 33.24) * mm});
            skArc(sketch, "E163", {"start": v(7.83, 36.95) * mm, "mid": v(7.75, 36.06) * mm, "end": v(7.83, 35.18) * mm});
            skArc(sketch, "E164", {"start": v(7.6, 38.67) * mm, "mid": v(7.14, 37.73) * mm, "end": v(7.83, 36.95) * mm});
            skArc(sketch, "E165", {"start": v(8.81, 38.54) * mm, "mid": v(8.7, 38.77) * mm, "end": v(8.44, 38.79) * mm});
            skLineSegment(sketch, "E166", {"start": v(8.44, 38.79) * mm, "end": v(7.96, 38) * mm});
            skLineSegment(sketch, "E167", {"start": v(8.81, 38.54) * mm, "end": v(8.33, 37.75) * mm});
            skArc(sketch, "E168", {"start": v(7.96, 38) * mm, "mid": v(8.02, 37.69) * mm, "end": v(8.33, 37.75) * mm});
            skArc(sketch, "E169", {"start": v(16.34, 39.67) * mm, "mid": v(14.4, 40.5) * mm, "end": v(12.3, 40.52) * mm});
            skArc(sketch, "E170", {"start": v(18.1, 35.72) * mm, "mid": v(17.72, 37.92) * mm, "end": v(16.34, 39.67) * mm});
            skLineSegment(sketch, "E171", {"start": v(18.1, 35.72) * mm, "end": v(16.89, 36.27) * mm});
            skArc(sketch, "E172", {"start": v(16.89, 36.27) * mm, "mid": v(16.7, 37.5) * mm, "end": v(16.05, 38.54) * mm});
            skArc(sketch, "E173", {"start": v(16.05, 38.54) * mm, "mid": v(15.9, 38.59) * mm, "end": v(15.77, 38.54) * mm});
            skLineSegment(sketch, "E174", {"start": v(15.77, 38.54) * mm, "end": v(14.41, 37.85) * mm});
            skArc(sketch, "E175", {"start": v(12.3, 40.52) * mm, "mid": v(12.48, 40.03) * mm, "end": v(12.77, 39.6) * mm});
            skArc(sketch, "E176", {"start": v(12.77, 39.6) * mm, "mid": v(13.55, 38.68) * mm, "end": v(14.41, 37.85) * mm});
            skArc(sketch, "E177", {"start": v(11.79, 40.39) * mm, "mid": v(12.25, 39.5) * mm, "end": v(12.85, 38.69) * mm});
            skArc(sketch, "E178", {"start": v(12.85, 38.69) * mm, "mid": v(13.49, 38.03) * mm, "end": v(14.19, 37.43) * mm});
            skArc(sketch, "E179", {"start": v(14.19, 37.43) * mm, "mid": v(14.23, 37.25) * mm, "end": v(14.3, 37.07) * mm});
            skArc(sketch, "E180", {"start": v(14.3, 37.07) * mm, "mid": v(14.78, 36.14) * mm, "end": v(15.4, 35.29) * mm});
            skArc(sketch, "E181", {"start": v(15.4, 35.29) * mm, "mid": v(15.9, 35) * mm, "end": v(16.46, 35.17) * mm});
            skArc(sketch, "E182", {"start": v(16.46, 35.17) * mm, "mid": v(16.7, 35.43) * mm, "end": v(16.86, 35.75) * mm});
            skLineSegment(sketch, "E183", {"start": v(16.86, 35.75) * mm, "end": v(17.98, 35.24) * mm});
            skArc(sketch, "E184", {"start": v(16.7, 33.6) * mm, "mid": v(17.5, 34.3) * mm, "end": v(17.98, 35.24) * mm});
            skArc(sketch, "E185", {"start": v(14.62, 32.92) * mm, "mid": v(15.7, 33.14) * mm, "end": v(16.7, 33.6) * mm});
            skArc(sketch, "E186", {"start": v(11.82, 32.97) * mm, "mid": v(13.22, 32.87) * mm, "end": v(14.62, 32.92) * mm});
            skArc(sketch, "E187", {"start": v(9.6, 33.95) * mm, "mid": v(10.64, 33.3) * mm, "end": v(11.82, 32.97) * mm});
            skArc(sketch, "E188", {"start": v(8.68, 35.7) * mm, "mid": v(8.98, 34.73) * mm, "end": v(9.6, 33.95) * mm});
            skArc(sketch, "E189", {"start": v(9.05, 38) * mm, "mid": v(8.7, 36.87) * mm, "end": v(8.68, 35.7) * mm});
            skArc(sketch, "E190", {"start": v(11.79, 40.39) * mm, "mid": v(10.18, 39.47) * mm, "end": v(9.05, 38) * mm});
            skArc(sketch, "E191", {"start": v(12.27, 37.88) * mm, "mid": v(11.66, 38.23) * mm, "end": v(11.04, 38.54) * mm});
            skArc(sketch, "E192", {"start": v(12.52, 37.26) * mm, "mid": v(12.5, 37.61) * mm, "end": v(12.27, 37.88) * mm});
            skArc(sketch, "E193", {"start": v(11.37, 35.33) * mm, "mid": v(12.01, 36.26) * mm, "end": v(12.52, 37.26) * mm});
            skArc(sketch, "E194", {"start": v(10.81, 35) * mm, "mid": v(11.13, 35.1) * mm, "end": v(11.37, 35.33) * mm});
            skArc(sketch, "E195", {"start": v(10.13, 35.28) * mm, "mid": v(10.44, 35.06) * mm, "end": v(10.81, 35) * mm});
            skArc(sketch, "E196", {"start": v(9.85, 35.75) * mm, "mid": v(9.96, 35.5) * mm, "end": v(10.13, 35.28) * mm});
            skArc(sketch, "E197", {"start": v(9.94, 37.26) * mm, "mid": v(9.81, 36.51) * mm, "end": v(9.85, 35.75) * mm});
            skArc(sketch, "E198", {"start": v(10.66, 38.56) * mm, "mid": v(10.2, 37.97) * mm, "end": v(9.94, 37.26) * mm});
            skArc(sketch, "E199", {"start": v(11.04, 38.54) * mm, "mid": v(10.85, 38.6) * mm, "end": v(10.66, 38.56) * mm});
            skCircle(sketch, "E200", {"center": v(11.71, 37.2) * mm, "radius": 0.34 * mm});
            skArc(sketch, "E201", {"start": v(12.8, 35.22) * mm, "mid": v(13.3, 35.1) * mm, "end": v(13.8, 35.18) * mm});
            skArc(sketch, "E202", {"start": v(13.44, 34.25) * mm, "mid": v(13.77, 34.36) * mm, "end": v(14.03, 34.58) * mm});
            skArc(sketch, "E203", {"start": v(13.04, 34.28) * mm, "mid": v(13.24, 34.25) * mm, "end": v(13.44, 34.25) * mm});
            skArc(sketch, "E204", {"start": v(12.48, 34.75) * mm, "mid": v(12.72, 34.47) * mm, "end": v(13.04, 34.28) * mm});
            skArc(sketch, "E205", {"start": v(12.48, 35.16) * mm, "mid": v(12.44, 34.96) * mm, "end": v(12.48, 34.75) * mm});
            skArc(sketch, "E206", {"start": v(12.6, 35.28) * mm, "mid": v(12.53, 35.23) * mm, "end": v(12.48, 35.16) * mm});
            skArc(sketch, "E207", {"start": v(12.8, 35.22) * mm, "mid": v(12.7, 35.26) * mm, "end": v(12.6, 35.28) * mm});
            skArc(sketch, "E208", {"start": v(14.03, 34.58) * mm, "mid": v(14.13, 34.7) * mm, "end": v(14.2, 34.86) * mm});
            skArc(sketch, "E209", {"start": v(14.2, 34.86) * mm, "mid": v(14.22, 35.03) * mm, "end": v(14.16, 35.2) * mm});
            skArc(sketch, "E210", {"start": v(14.16, 35.2) * mm, "mid": v(14.11, 35.26) * mm, "end": v(14.03, 35.27) * mm});
            skArc(sketch, "E211", {"start": v(13.8, 35.18) * mm, "mid": v(13.92, 35.22) * mm, "end": v(14.03, 35.27) * mm});
            skSolve(sketch);
        }
        {
            var Q0;
            Q0=makeQuery(id+"F7.imprint","IMPRINT",FACE,{"disambiguationData":[TD([[makeQuery(id+"F7.imprint","IMPRINT",EDGE,{"derivedFrom":sQuery(id+"F7.wireOp",EDGE,"E151")}),1.0]])]});
            var Q1;
            Q1=makeQuery(id+"F7.imprint","IMPRINT",FACE,{"disambiguationData":[TD([[makeQuery(id+"F7.imprint","IMPRINT",EDGE,{"derivedFrom":sQuery(id+"F7.wireOp",EDGE,"E191")}),1.0]])]});
            var Q2;
            Q2=makeQuery(id+"F7.imprint","IMPRINT",FACE,{"disambiguationData":[TD([[makeQuery(id+"F7.imprint","IMPRINT",EDGE,{"derivedFrom":sQuery(id+"F7.wireOp",EDGE,"E201")}),-1.0]])]});
            extrude(context, id + "F8", {"entities" : qUnion([Q0, Q1, Q2]), "operationType" : NewBodyOperationType.ADD, "depth" : 2 * mm, "offsetDistance" : 25.4 * mm});
        }
        {
            var Q0;
            {var subQ12=sQuery(id+"F4.wireOp",EDGE,"E136");Q0=makeQuery(id+"F8.boolean.opBoolean","SPLIT",FACE,{"disambiguationData":[TD([makeQuery(id+"F5.opExtrude","SWEPT_FACE",FACE,{"disambiguationData":[OSD([subQ12])]})])],"derivedFrom":makeQuery(id+"F1.opExtrude","CAP_FACE",FACE,{"disambiguationData":[OSD([sQuery(id+"F0.wireOp",EDGE,"E0.bottom"),sQuery(id+"F0.wireOp",EDGE,"E0.top"),sQuery(id+"F0.wireOp",EDGE,"E0.left"),sQuery(id+"F0.wireOp",EDGE,"E2"),sQuery(id+"F0.wireOp",EDGE,"E3"),sQuery(id+"F0.wireOp",EDGE,"E4"),sQuery(id+"F0.wireOp",EDGE,"E5"),sQuery(id+"F0.wireOp",EDGE,"E6"),sQuery(id+"F0.wireOp",EDGE,"E7"),sQuery(id+"F0.wireOp",EDGE,"E8"),sQuery(id+"F0.wireOp",EDGE,"E9"),sQuery(id+"F0.wireOp",EDGE,"E10"),sQuery(id+"F0.wireOp",EDGE,"E11"),sQuery(id+"F0.wireOp",EDGE,"E12"),sQuery(id+"F0.wireOp",EDGE,"E13.trimOffspring"),sQuery(id+"F0.wireOp",EDGE,"E14"),sQuery(id+"F0.wireOp",EDGE,"E15"),sQuery(id+"F0.wireOp",EDGE,"E22"),sQuery(id+"F0.wireOp",EDGE,"E23"),sQuery(id+"F0.wireOp",EDGE,"E24")])],"isStart":false})});}
            var sketch = newSketch(context, id + "F9", { "sketchPlane" : qUnion([Q0])});
            skLineSegment(sketch, "E212", {"start": v(13.08, 43.87) * mm, "end": v(8.9, 44.6) * mm});
            skLineSegment(sketch, "E213", {"start": v(13.34, 43.87) * mm, "end": v(17.52, 44.6) * mm});
            skSolve(sketch);
        }
        {
            var Q0;
            {var subQ0=sQuery(id+"F9.wireOp",EDGE,"E212");Q0=makeQuery(id+"F9.imprint","IMPRINT",FACE,{"disambiguationData":[TD([[makeQuery(id+"F9.imprint","IMPRINT",EDGE,{"derivedFrom":subQ0}),-1.0]])]});}
            var Q1;
            {var subQ0=sQuery(id+"F9.wireOp",EDGE,"E213");Q1=makeQuery(id+"F9.imprint","IMPRINT",FACE,{"disambiguationData":[TD([[makeQuery(id+"F9.imprint","IMPRINT",EDGE,{"derivedFrom":subQ0}),1.0]])]});}
            extrude(context, id + "F10", {"entities" : qUnion([Q0, Q1]), "operationType" : NewBodyOperationType.REMOVE, "oppositeDirection" : true, "depth" : 25.4 * mm, "offsetDistance" : 25.4 * mm});
        }
    });
